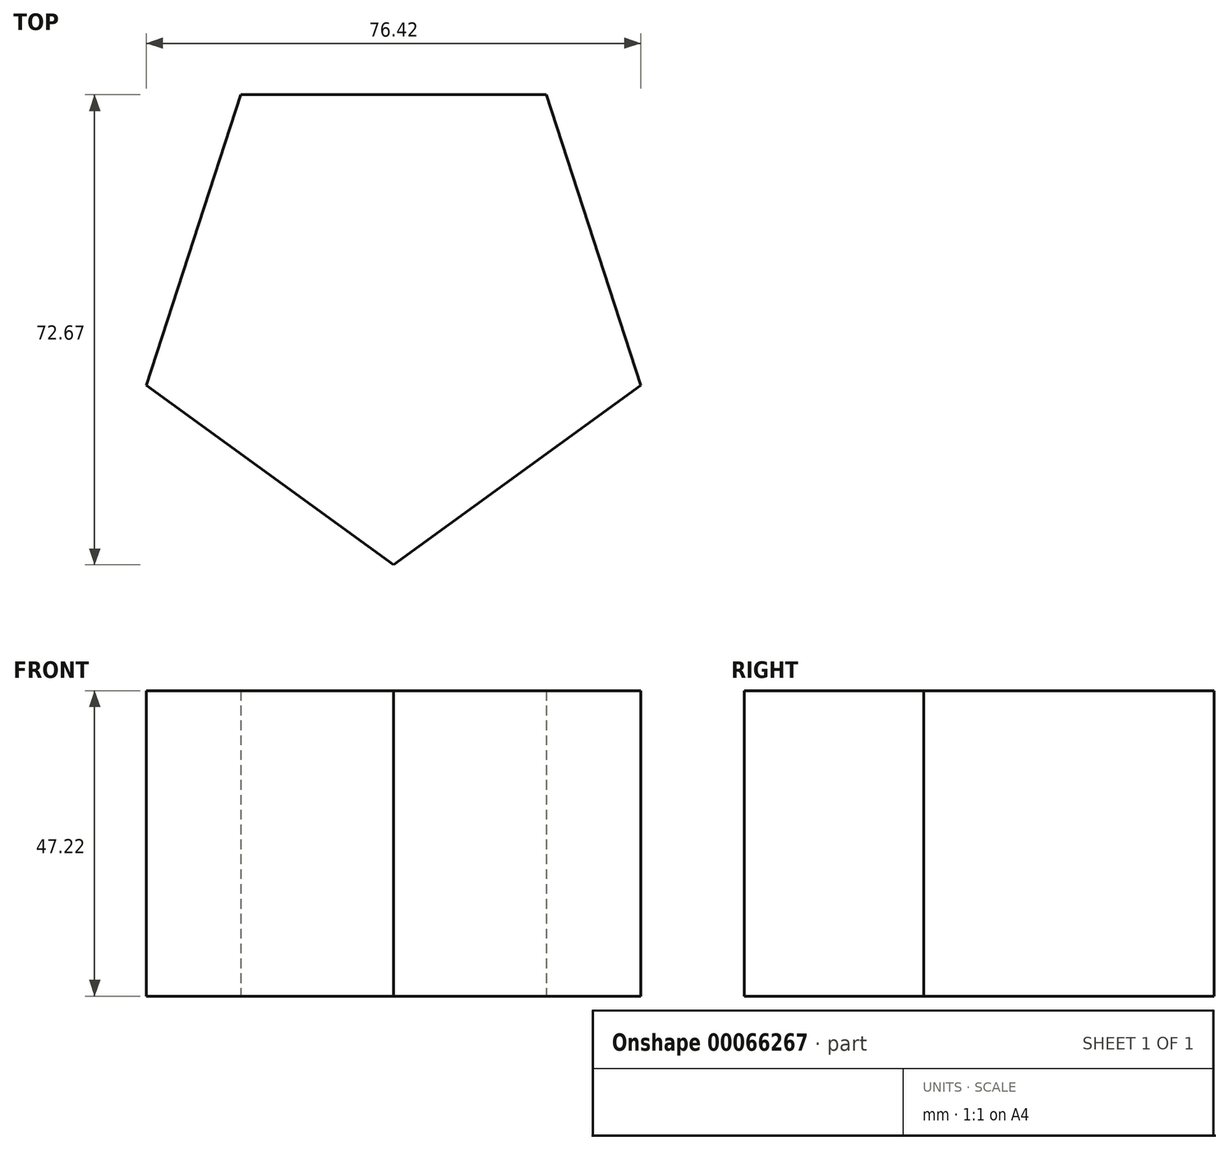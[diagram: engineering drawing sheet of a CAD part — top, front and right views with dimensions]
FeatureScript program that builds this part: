
annotation { "Feature Type Name" : "Feature", "Feature Type Description" : "" }
export const myFeature = defineFeature(function(context is Context, id is Id, definition is map)
    precondition{}
    {
        {
            var Q0;
            Q0=qCreatedBy(makeId("Top.planeOp"),FACE);
            var sketch = newSketch(context, id + "F0", { "sketchPlane" : qUnion([Q0])});
            skCircle(sketch, "E0.cCircle", {"center": v(0, 0) * mm, "radius": 32.5 * mm, "construction": true});
            skLineSegment(sketch, "E0.0", {"start": v(-23.61, 32.5) * mm, "end": v(23.61, 32.5) * mm});
            skLineSegment(sketch, "E0.1", {"start": v(23.61, 32.5) * mm, "end": v(38.2, -12.41) * mm});
            skLineSegment(sketch, "E0.2", {"start": v(38.2, -12.41) * mm, "end": v(0, -40.17) * mm});
            skLineSegment(sketch, "E0.3", {"start": v(0, -40.17) * mm, "end": v(-38.2, -12.41) * mm});
            skLineSegment(sketch, "E0.4", {"start": v(-38.2, -12.41) * mm, "end": v(-23.61, 32.5) * mm});
            skPoint(sketch, "E0.0.midPoint", {"position": v(0, 32.5) * mm});
            skSolve(sketch);
        }
        {
            var Q0;
            Q0=makeQuery(id+"F0.imprint","IMPRINT",FACE,{"disambiguationData":[TD([[makeQuery(id+"F0.imprint","IMPRINT",EDGE,{"derivedFrom":sQuery(id+"F0.wireOp",EDGE,"E0.0")}),-1.0]])]});
            extrude(context, id + "F1", {"entities" : qUnion([Q0]), "endBound" : BoundingType.SYMMETRIC, "depth" : 47.23 * mm});
        }
    });
